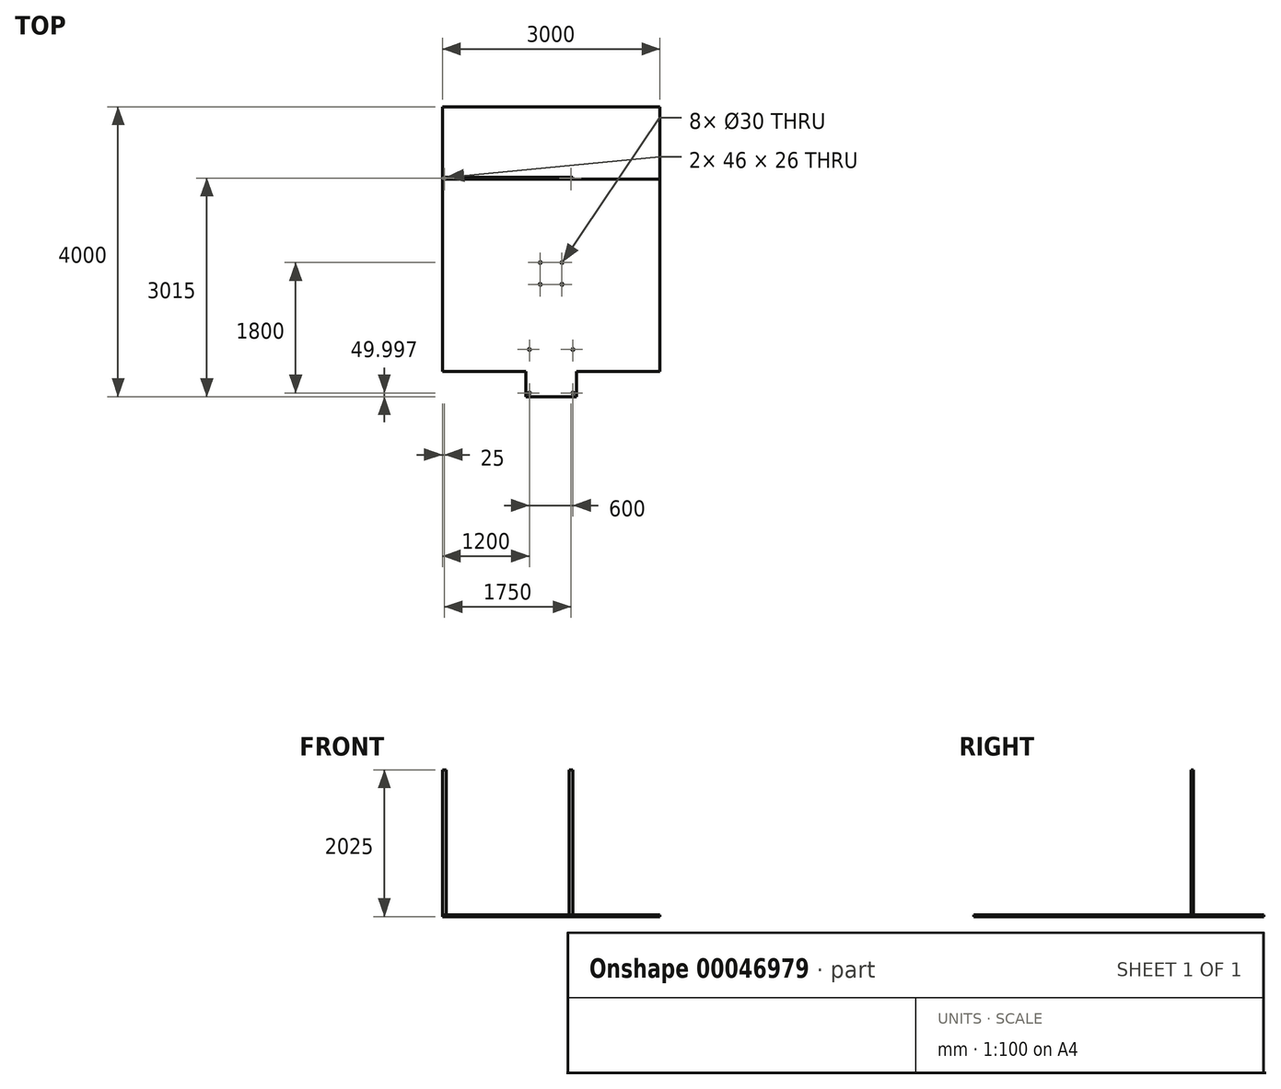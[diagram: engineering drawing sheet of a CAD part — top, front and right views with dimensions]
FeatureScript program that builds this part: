
annotation { "Feature Type Name" : "Feature", "Feature Type Description" : "" }
export const myFeature = defineFeature(function(context is Context, id is Id, definition is map)
    precondition{}
    {
        {
            var Q0;
            Q0=qCreatedBy(makeId("Top.planeOp"),FACE);
            var sketch = newSketch(context, id + "F0", { "sketchPlane" : qUnion([Q0])});
            skLineSegment(sketch, "E0.rect.bottom", {"start": v(-350, -406.83) * mm, "end": v(350, -406.83) * mm});
            skLineSegment(sketch, "E0.rect.top", {"start": v(-350, 293.17) * mm, "end": v(350, 293.17) * mm});
            skLineSegment(sketch, "E0.rect.left", {"start": v(-350, -406.83) * mm, "end": v(-350, 293.17) * mm});
            skLineSegment(sketch, "E0.rect.right", {"start": v(350, -406.83) * mm, "end": v(350, 293.17) * mm});
            skPoint(sketch, "E0.rect.middle", {"position": v(0, -56.83) * mm});
            skLineSegment(sketch, "E1.rect.bottom", {"start": v(-300, 243.17) * mm, "end": v(300, 243.17) * mm, "construction": true});
            skLineSegment(sketch, "E1.rect.top", {"start": v(-300, -356.83) * mm, "end": v(300, -356.83) * mm, "construction": true});
            skLineSegment(sketch, "E1.rect.left", {"start": v(-300, 243.17) * mm, "end": v(-300, -356.83) * mm, "construction": true});
            skLineSegment(sketch, "E1.rect.right", {"start": v(300, 243.17) * mm, "end": v(300, -356.83) * mm, "construction": true});
            skCircle(sketch, "E2", {"center": v(-300, 243.17) * mm, "radius": 15 * mm});
            skCircle(sketch, "E3", {"center": v(300, 243.17) * mm, "radius": 15 * mm});
            skCircle(sketch, "E4", {"center": v(300, -356.83) * mm, "radius": 15 * mm});
            skCircle(sketch, "E5", {"center": v(-300, -356.83) * mm, "radius": 15 * mm});
            skLineSegment(sketch, "E6", {"start": v(-350, -406.83) * mm, "end": v(-1500, -406.83) * mm});
            skLineSegment(sketch, "E7", {"start": v(-1500, -406.83) * mm, "end": v(-1500, 2593.17) * mm});
            skLineSegment(sketch, "E8", {"start": v(-1500, 2593.17) * mm, "end": v(0, 2593.17) * mm});
            skLineSegment(sketch, "E9.MirrorCS", {"start": v(1500, 2593.17) * mm, "end": v(0, 2593.17) * mm});
            skLineSegment(sketch, "E10.MirrorCS", {"start": v(1500, -406.83) * mm, "end": v(1500, 2593.17) * mm});
            skLineSegment(sketch, "E11.MirrorCS", {"start": v(300, 243.17) * mm, "end": v(-300, 243.17) * mm});
            skLineSegment(sketch, "E12.MirrorCS", {"start": v(300, -356.83) * mm, "end": v(-300, -356.83) * mm});
            skLineSegment(sketch, "E13.MirrorCS", {"start": v(300, 243.17) * mm, "end": v(300, -356.83) * mm});
            skLineSegment(sketch, "E14.MirrorCS", {"start": v(-300, 243.17) * mm, "end": v(-300, -356.83) * mm});
            skLineSegment(sketch, "E15.MirrorCS", {"start": v(350, -406.83) * mm, "end": v(1500, -406.83) * mm});
            skSolve(sketch);
        }
        {
            var Q0;
            Q0=qSketchRegion(id+"F0",true);
            var Q1;
            {var subQ11=sQuery(id+"F0.wireOp",EDGE,"E2");var subQ13=sQuery(id+"F0.wireOp",EDGE,"E11.MirrorCS");var subQ15=makeQuery(id+"F0.imprint","INTERSECT",VERTEX,{"derivedFrom":[subQ11,subQ13]});Q1=makeQuery(id+"F0.imprint","IMPRINT",FACE,{"disambiguationData":[TD([[makeQuery(id+"F0.imprint","IMPRINT",EDGE,{"disambiguationData":[TD([[subQ15,1.0]])],"derivedFrom":subQ11}),-1.0]])]});}
            extrude(context, id + "F1", {"entities" : qUnion([Q0, Q1]), "depth" : 25 * mm});
        }
        {
            var Q0;
            Q0=makeQuery(id+"F1.opExtrude","CAP_FACE",FACE,{"disambiguationData":[OSD([sQuery(id+"F0.wireOp",EDGE,"E0.rect.bottom"),sQuery(id+"F0.wireOp",EDGE,"E2"),sQuery(id+"F0.wireOp",EDGE,"E5"),sQuery(id+"F0.wireOp",EDGE,"E6"),sQuery(id+"F0.wireOp",EDGE,"E7"),sQuery(id+"F0.wireOp",EDGE,"E8"),sQuery(id+"F0.wireOp",EDGE,"E3"),sQuery(id+"F0.wireOp",EDGE,"E4"),sQuery(id+"F0.wireOp",EDGE,"E9.MirrorCS"),sQuery(id+"F0.wireOp",EDGE,"E10.MirrorCS"),sQuery(id+"F0.wireOp",EDGE,"E15.MirrorCS")])],"isStart":false});
            var sketch = newSketch(context, id + "F2", { "sketchPlane" : qUnion([Q0])});
            skLineSegment(sketch, "E16", {"start": v(0, 0) * mm, "end": v(0, 1550) * mm, "construction": true});
            skLineSegment(sketch, "E17", {"start": v(0, 775) * mm, "end": v(145.88, 775) * mm, "construction": true});
            skCircle(sketch, "E18", {"center": v(-300, 243.17) * mm, "radius": 15 * mm});
            skCircle(sketch, "E19", {"center": v(300, 243.17) * mm, "radius": 15 * mm});
            skCircle(sketch, "E20", {"center": v(-300, -356.83) * mm, "radius": 15 * mm});
            skCircle(sketch, "E21", {"center": v(300, -356.83) * mm, "radius": 15 * mm});
            skSolve(sketch);
        }
        {
            var Q0;
            Q0=qSketchRegion(id+"F2",true);
            extrude(context, id + "F3", {"entities" : qUnion([Q0]), "operationType" : NewBodyOperationType.REMOVE, "oppositeDirection" : true, "depth" : 25 * mm});
        }
        {
            var Q0;
            Q0=makeQuery(id+"F1.opExtrude","CAP_FACE",FACE,{"disambiguationData":[OSD([sQuery(id+"F0.wireOp",EDGE,"E0.rect.bottom"),sQuery(id+"F0.wireOp",EDGE,"E2"),sQuery(id+"F0.wireOp",EDGE,"E5"),sQuery(id+"F0.wireOp",EDGE,"E6"),sQuery(id+"F0.wireOp",EDGE,"E7"),sQuery(id+"F0.wireOp",EDGE,"E8"),sQuery(id+"F0.wireOp",EDGE,"E3"),sQuery(id+"F0.wireOp",EDGE,"E4"),sQuery(id+"F0.wireOp",EDGE,"E9.MirrorCS"),sQuery(id+"F0.wireOp",EDGE,"E10.MirrorCS"),sQuery(id+"F0.wireOp",EDGE,"E15.MirrorCS")])],"isStart":false});
            var sketch = newSketch(context, id + "F4", { "sketchPlane" : qUnion([Q0])});
            skLineSegment(sketch, "E22", {"start": v(-300, 243.17) * mm, "end": v(285, 243.17) * mm, "construction": true});
            skLineSegment(sketch, "E23", {"start": v(0, 243.17) * mm, "end": v(0, 1143.17) * mm, "construction": true});
            skPoint(sketch, "E24.orphan", {"position": v(0, 82.08) * mm});
            skLineSegment(sketch, "E25", {"start": v(0, 1143.17) * mm, "end": v(-150, 1143.17) * mm, "construction": true});
            skLineSegment(sketch, "E26", {"start": v(-150, 1143.17) * mm, "end": v(-150, 1443.17) * mm, "construction": true});
            skLineSegment(sketch, "E27", {"start": v(-150, 1443.17) * mm, "end": v(0, 1443.17) * mm, "construction": true});
            skLineSegment(sketch, "E28.MirrorCS", {"start": v(150, 1143.17) * mm, "end": v(150, 1443.17) * mm, "construction": true});
            skLineSegment(sketch, "E29.MirrorCS", {"start": v(0, 1143.17) * mm, "end": v(150, 1143.17) * mm, "construction": true});
            skLineSegment(sketch, "E30.MirrorCS", {"start": v(150, 1443.17) * mm, "end": v(0, 1443.17) * mm, "construction": true});
            skCircle(sketch, "E31", {"center": v(-150, 1443.17) * mm, "radius": 15 * mm});
            skCircle(sketch, "E32", {"center": v(150, 1443.17) * mm, "radius": 15 * mm});
            skCircle(sketch, "E33", {"center": v(150, 1143.17) * mm, "radius": 15 * mm});
            skCircle(sketch, "E34", {"center": v(-150, 1143.17) * mm, "radius": 15 * mm});
            skSolve(sketch);
        }
        {
            var Q0;
            Q0=qSketchRegion(id+"F4",true);
            extrude(context, id + "F5", {"entities" : qUnion([Q0]), "operationType" : NewBodyOperationType.REMOVE, "oppositeDirection" : true, "depth" : 50 * mm});
        }
        {
            var Q0;
            Q0=makeQuery(id+"F1.opExtrude","CAP_FACE",FACE,{"disambiguationData":[OSD([sQuery(id+"F0.wireOp",EDGE,"E0.rect.bottom"),sQuery(id+"F0.wireOp",EDGE,"E2"),sQuery(id+"F0.wireOp",EDGE,"E5"),sQuery(id+"F0.wireOp",EDGE,"E6"),sQuery(id+"F0.wireOp",EDGE,"E7"),sQuery(id+"F0.wireOp",EDGE,"E8"),sQuery(id+"F0.wireOp",EDGE,"E3"),sQuery(id+"F0.wireOp",EDGE,"E4"),sQuery(id+"F0.wireOp",EDGE,"E9.MirrorCS"),sQuery(id+"F0.wireOp",EDGE,"E10.MirrorCS"),sQuery(id+"F0.wireOp",EDGE,"E15.MirrorCS")])],"isStart":false});
            var sketch = newSketch(context, id + "F6", { "sketchPlane" : qUnion([Q0])});
            skLineSegment(sketch, "E35", {"start": v(0, 0) * mm, "end": v(0, -406.83) * mm, "construction": true});
            skLineSegment(sketch, "E36.rect.bottom", {"start": v(0, -406.83) * mm, "end": v(0, -406.83) * mm});
            skLineSegment(sketch, "E36.rect.left", {"start": v(0, -406.83) * mm, "end": v(0, -406.83) * mm});
            skLineSegment(sketch, "E36.rect.right", {"start": v(0, -406.83) * mm, "end": v(0, -406.83) * mm});
            skPoint(sketch, "E36.rect.middle", {"position": v(0, -406.83) * mm});
            skLineSegment(sketch, "E37", {"start": v(-350, -406.83) * mm, "end": v(-350, -56.83) * mm});
            skPoint(sketch, "E38.endSnap0", {"position": v(0, -203.42) * mm});
            skLineSegment(sketch, "E39", {"start": v(-350, -56.83) * mm, "end": v(-1500, -56.83) * mm});
            skLineSegment(sketch, "E40", {"start": v(-350, -406.83) * mm, "end": v(-1500, -406.83) * mm});
            skLineSegment(sketch, "E41", {"start": v(-1500, -406.83) * mm, "end": v(-1500, -56.83) * mm});
            skLineSegment(sketch, "E42.MirrorCS", {"start": v(350, -56.83) * mm, "end": v(1500, -56.83) * mm});
            skLineSegment(sketch, "E43.MirrorCS", {"start": v(350, -406.83) * mm, "end": v(350, -56.83) * mm});
            skLineSegment(sketch, "E44.MirrorCS", {"start": v(350, -406.83) * mm, "end": v(1500, -406.83) * mm});
            skLineSegment(sketch, "E45.MirrorCS", {"start": v(1500, -406.83) * mm, "end": v(1500, -56.83) * mm});
            skSolve(sketch);
        }
        {
            var Q0;
            Q0=qSketchRegion(id+"F6",true);
            extrude(context, id + "F7", {"entities" : qUnion([Q0]), "operationType" : NewBodyOperationType.REMOVE, "oppositeDirection" : true, "depth" : 25 * mm});
        }
        {
            var Q0;
            Q0=makeQuery(id+"F1.opExtrude","CAP_FACE",FACE,{"disambiguationData":[OSD([sQuery(id+"F0.wireOp",EDGE,"E0.rect.bottom"),sQuery(id+"F0.wireOp",EDGE,"E2"),sQuery(id+"F0.wireOp",EDGE,"E5"),sQuery(id+"F0.wireOp",EDGE,"E6"),sQuery(id+"F0.wireOp",EDGE,"E7"),sQuery(id+"F0.wireOp",EDGE,"E8"),sQuery(id+"F0.wireOp",EDGE,"E3"),sQuery(id+"F0.wireOp",EDGE,"E4"),sQuery(id+"F0.wireOp",EDGE,"E9.MirrorCS"),sQuery(id+"F0.wireOp",EDGE,"E10.MirrorCS"),sQuery(id+"F0.wireOp",EDGE,"E15.MirrorCS")])],"isStart":false});
            var sketch = newSketch(context, id + "F8", { "sketchPlane" : qUnion([Q0])});
            skLineSegment(sketch, "E46", {"start": v(-1500, 2593.17) * mm, "end": v(1500, 2593.17) * mm});
            skLineSegment(sketch, "E47", {"start": v(1500, 2593.17) * mm, "end": v(1500, 3593.17) * mm});
            skLineSegment(sketch, "E48", {"start": v(1500, 3593.17) * mm, "end": v(-1500, 3593.17) * mm});
            skLineSegment(sketch, "E49", {"start": v(-1500, 3593.17) * mm, "end": v(-1500, 2593.17) * mm});
            skSolve(sketch);
        }
        {
            var Q0;
            Q0=qSketchRegion(id+"F8",true);
            extrude(context, id + "F9", {"entities" : qUnion([Q0]), "oppositeDirection" : true, "depth" : 25 * mm});
        }
        {
            var Q0;
            Q0=makeQuery(id+"F8.imprint","IMPRINT",FACE,{"disambiguationData":[TD([[makeQuery(id+"F8.imprint","IMPRINT",EDGE,{"derivedFrom":sQuery(id+"F8.wireOp",EDGE,"E46")}),-1.0]])]});
            var sketch = newSketch(context, id + "F10", { "sketchPlane" : qUnion([Q0])});
            skLineSegment(sketch, "E50.bottom", {"start": v(-1500, 2593.17) * mm, "end": v(-1450, 2593.17) * mm});
            skLineSegment(sketch, "E50.top", {"start": v(-1500, 2623.17) * mm, "end": v(-1450, 2623.17) * mm});
            skLineSegment(sketch, "E50.left", {"start": v(-1500, 2593.17) * mm, "end": v(-1500, 2623.17) * mm});
            skLineSegment(sketch, "E50.right", {"start": v(-1450, 2593.17) * mm, "end": v(-1450, 2623.17) * mm});
            skLineSegment(sketch, "E51.bottom", {"start": v(-1498, 2595.17) * mm, "end": v(-1452, 2595.17) * mm});
            skLineSegment(sketch, "E51.top", {"start": v(-1498, 2621.17) * mm, "end": v(-1452, 2621.17) * mm});
            skLineSegment(sketch, "E51.left", {"start": v(-1498, 2595.17) * mm, "end": v(-1498, 2621.17) * mm});
            skLineSegment(sketch, "E51.right", {"start": v(-1452, 2595.17) * mm, "end": v(-1452, 2621.17) * mm});
            skLineSegment(sketch, "E52", {"start": v(-1500, 2663.4) * mm, "end": v(-600, 2663.4) * mm, "construction": true});
            skLineSegment(sketch, "E53", {"start": v(-600, 2663.4) * mm, "end": v(-600, 2595.97) * mm, "construction": true});
            skLineSegment(sketch, "E54.MirrorCS", {"start": v(300, 2593.17) * mm, "end": v(300, 2623.17) * mm});
            skLineSegment(sketch, "E55.MirrorCS", {"start": v(252, 2595.17) * mm, "end": v(252, 2621.17) * mm});
            skLineSegment(sketch, "E56.MirrorCS", {"start": v(298, 2595.17) * mm, "end": v(298, 2621.17) * mm});
            skLineSegment(sketch, "E57.MirrorCS", {"start": v(250, 2593.17) * mm, "end": v(250, 2623.17) * mm});
            skLineSegment(sketch, "E58.MirrorCS", {"start": v(300, 2623.17) * mm, "end": v(250, 2623.17) * mm});
            skLineSegment(sketch, "E59.MirrorCS", {"start": v(298, 2621.17) * mm, "end": v(252, 2621.17) * mm});
            skLineSegment(sketch, "E60.MirrorCS", {"start": v(298, 2595.17) * mm, "end": v(252, 2595.17) * mm});
            skLineSegment(sketch, "E61.MirrorCS", {"start": v(300, 2593.17) * mm, "end": v(250, 2593.17) * mm});
            skSolve(sketch);
        }
        {
            var Q0;
            Q0=qSketchRegion(id+"F10",true);
            extrude(context, id + "F11", {"entities" : qUnion([Q0]), "depth" : 2000 * mm});
        }
        {
            var Q0;
            Q0=makeQuery(id+"F8.imprint","IMPRINT",FACE,{"disambiguationData":[TD([[makeQuery(id+"F8.imprint","IMPRINT",EDGE,{"derivedFrom":sQuery(id+"F8.wireOp",EDGE,"E46")}),-1.0]])]});
            var sketch = newSketch(context, id + "F12", { "sketchPlane" : qUnion([Q0])});
            skLineSegment(sketch, "E62.bottom", {"start": v(-1450, 2593.17) * mm, "end": v(250, 2593.17) * mm});
            skLineSegment(sketch, "E62.top", {"start": v(-1450, 2623.17) * mm, "end": v(250, 2623.17) * mm});
            skLineSegment(sketch, "E62.left", {"start": v(-1450, 2593.17) * mm, "end": v(-1450, 2623.17) * mm});
            skLineSegment(sketch, "E62.right", {"start": v(250, 2593.17) * mm, "end": v(250, 2623.17) * mm});
            skSolve(sketch);
        }
        {
            var Q0;
            Q0=qSketchRegion(id+"F12",true);
            extrude(context, id + "F13", {"entities" : qUnion([Q0]), "operationType" : NewBodyOperationType.REMOVE, "oppositeDirection" : true, "depth" : 10 * mm});
        }
    });
